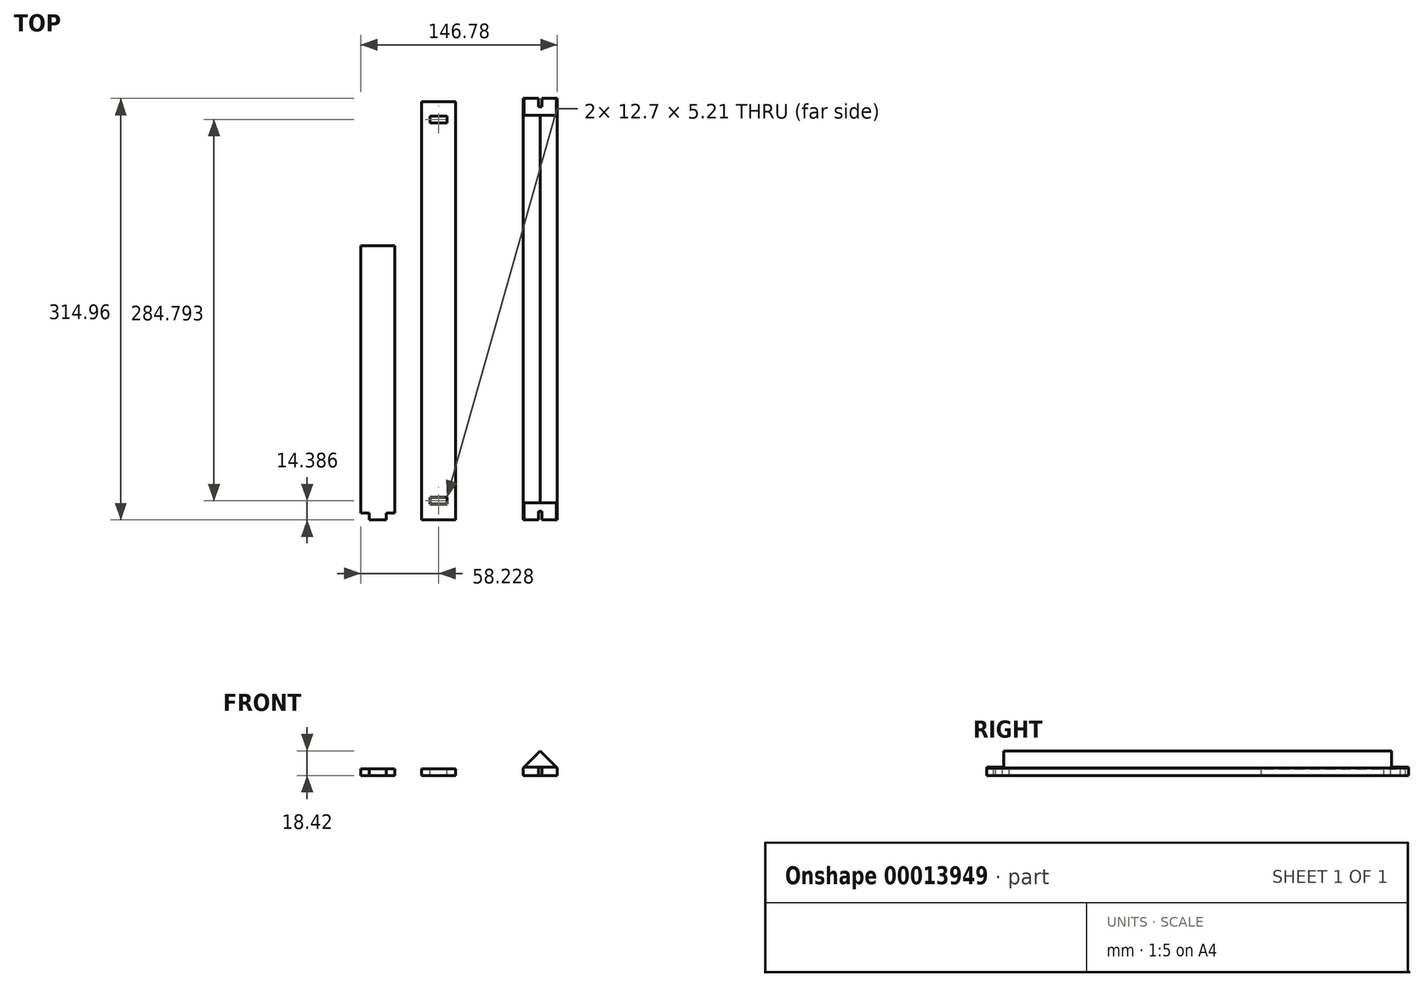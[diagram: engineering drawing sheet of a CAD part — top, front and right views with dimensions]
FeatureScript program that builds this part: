
annotation { "Feature Type Name" : "Feature", "Feature Type Description" : "" }
export const myFeature = defineFeature(function(context is Context, id is Id, definition is map)
    precondition{}
    {
        {
            var Q0;
            Q0=qCreatedBy(makeId("Front.planeOp"),FACE);
            var sketch = newSketch(context, id + "F0", { "sketchPlane" : qUnion([Q0])});
            skLineSegment(sketch, "E0.bottom", {"start": v(0, 0) * mm, "end": v(25.4, 0) * mm});
            skLineSegment(sketch, "E0.left", {"start": v(0, 0) * mm, "end": v(0, 5.72) * mm});
            skLineSegment(sketch, "E0.right", {"start": v(25.4, 0) * mm, "end": v(25.4, 5.72) * mm});
            skLineSegment(sketch, "E1", {"start": v(0, 5.71) * mm, "end": v(12.7, 18.42) * mm});
            skLineSegment(sketch, "E2", {"start": v(25.4, 5.72) * mm, "end": v(12.7, 18.42) * mm});
            skSolve(sketch);
        }
        {
            var Q0;
            Q0=makeQuery(id+"F0.imprint","IMPRINT",FACE,{"disambiguationData":[TD([[makeQuery(id+"F0.imprint","IMPRINT",EDGE,{"derivedFrom":sQuery(id+"F0.wireOp",EDGE,"E0.bottom")}),1.0]])]});
            extrude(context, id + "F1", {"entities" : qUnion([Q0]), "oppositeDirection" : true, "depth" : 314.96 * mm});
        }
        {
            var Q0;
            Q0=qCreatedBy(makeId("Top.planeOp"),FACE);
            cPlane(context, id + "F2", {"entities" : qUnion([Q0]), "cplaneType" : CPlaneType.OFFSET, "offset" : 25.4 * mm, "width" : 152.4 * mm, "height" : 152.4 * mm});
        }
        {
            var Q0;
            Q0=qCreatedBy(id+"F2.planeOp",FACE);
            var sketch = newSketch(context, id + "F3", { "sketchPlane" : qUnion([Q0])});
            skLineSegment(sketch, "E3.bottom", {"start": v(0, 0) * mm, "end": v(25.4, 0) * mm});
            skLineSegment(sketch, "E3.top", {"start": v(0, 12.7) * mm, "end": v(25.4, 12.7) * mm});
            skLineSegment(sketch, "E3.left", {"start": v(0, 0) * mm, "end": v(0, 12.7) * mm});
            skLineSegment(sketch, "E3.right", {"start": v(25.4, 0) * mm, "end": v(25.4, 12.7) * mm});
            skLineSegment(sketch, "E4.0", {"start": v(25.4, 314.96) * mm, "end": v(25.4, 0) * mm});
            skLineSegment(sketch, "E5.0", {"start": v(25.4, 314.96) * mm, "end": v(12.7, 314.96) * mm});
            skLineSegment(sketch, "E6.0", {"start": v(0, 314.96) * mm, "end": v(0, 0) * mm});
            skLineSegment(sketch, "E7.bottom", {"start": v(25.4, 314.96) * mm, "end": v(0, 314.96) * mm});
            skLineSegment(sketch, "E7.top", {"start": v(25.4, 302.26) * mm, "end": v(0, 302.26) * mm});
            skLineSegment(sketch, "E7.left", {"start": v(25.4, 314.96) * mm, "end": v(25.4, 302.26) * mm});
            skLineSegment(sketch, "E7.right", {"start": v(0, 314.96) * mm, "end": v(0, 302.26) * mm});
            skSolve(sketch);
        }
        {
            var Q0;
            Q0=makeQuery(id+"F3.imprint","IMPRINT",FACE,{"disambiguationData":[TD([[makeQuery(id+"F3.imprint","IMPRINT",EDGE,{"derivedFrom":sQuery(id+"F3.wireOp",EDGE,"E7.top")}),-1.0]])]});
            var Q1;
            {var subQ2=sQuery(id+"F3.wireOp",EDGE,"E3.bottom");Q1=makeQuery(id+"F3.imprint","IMPRINT",FACE,{"disambiguationData":[TD([[makeQuery(id+"F3.imprint","IMPRINT",EDGE,{"derivedFrom":subQ2}),1.0]])]});}
            var Q2;
            Q2=qCreatedBy(makeId("Top.planeOp"),FACE);
            extrude(context, id + "F4", {"entities" : qUnion([Q0, Q1]), "operationType" : NewBodyOperationType.REMOVE, "oppositeDirection" : true, "endBoundEntity" : qUnion([Q2]), "depth" : 19.05 * mm});
        }
        {
            var Q0;
            Q0=makeQuery(id+"F1.opExtrude","SWEPT_FACE",FACE,{"disambiguationData":[OSD([sQuery(id+"F0.wireOp",EDGE,"E0.bottom")])]});
            var sketch = newSketch(context, id + "F5", { "sketchPlane" : qUnion([Q0])});
            skLineSegment(sketch, "E8", {"start": v(12.7, 0) * mm, "end": v(12.7, -6.35) * mm, "construction": true});
            skLineSegment(sketch, "E9.rect.bottom", {"start": v(11.43, 0) * mm, "end": v(13.97, 0) * mm});
            skLineSegment(sketch, "E9.rect.top", {"start": v(11.43, -6.35) * mm, "end": v(13.97, -6.35) * mm});
            skLineSegment(sketch, "E9.rect.left", {"start": v(11.43, 0) * mm, "end": v(11.43, -6.35) * mm});
            skLineSegment(sketch, "E9.rect.right", {"start": v(13.97, 0) * mm, "end": v(13.97, -6.35) * mm});
            skPoint(sketch, "E9.rect.middle", {"position": v(12.7, -3.18) * mm});
            skLineSegment(sketch, "E10", {"start": v(12.7, -314.96) * mm, "end": v(12.7, -308.6) * mm, "construction": true});
            skPoint(sketch, "E11.rect.middle", {"position": v(12.7, -314.96) * mm});
            skLineSegment(sketch, "E12.rect.bottom", {"start": v(11.43, -314.96) * mm, "end": v(13.97, -314.96) * mm});
            skLineSegment(sketch, "E12.rect.top", {"start": v(11.43, -308.6) * mm, "end": v(13.97, -308.6) * mm});
            skLineSegment(sketch, "E12.rect.left", {"start": v(11.43, -314.96) * mm, "end": v(11.43, -308.6) * mm});
            skLineSegment(sketch, "E12.rect.right", {"start": v(13.97, -314.96) * mm, "end": v(13.97, -308.6) * mm});
            skPoint(sketch, "E12.rect.middle", {"position": v(12.7, -311.78) * mm});
            skSolve(sketch);
        }
        {
            var Q0;
            Q0=makeQuery(id+"F5.imprint","IMPRINT",FACE,{"disambiguationData":[TD([[makeQuery(id+"F5.imprint","IMPRINT",EDGE,{"derivedFrom":sQuery(id+"F5.wireOp",EDGE,"E12.rect.bottom")}),1.0]])]});
            var Q1;
            Q1=makeQuery(id+"F5.imprint","IMPRINT",FACE,{"disambiguationData":[TD([[makeQuery(id+"F5.imprint","IMPRINT",EDGE,{"derivedFrom":sQuery(id+"F5.wireOp",EDGE,"E9.rect.bottom")}),-1.0]])]});
            extrude(context, id + "F6", {"entities" : qUnion([Q0, Q1]), "operationType" : NewBodyOperationType.REMOVE, "endBound" : BoundingType.THROUGH_ALL, "oppositeDirection" : true, "depth" : 25.4 * mm});
        }
        {
            var Q0;
            Q0=qCreatedBy(makeId("Top.planeOp"),FACE);
            var sketch = newSketch(context, id + "F7", { "sketchPlane" : qUnion([Q0])});
            skLineSegment(sketch, "E13.bottom", {"start": v(-75.85, 0) * mm, "end": v(-50.45, 0) * mm});
            skLineSegment(sketch, "E13.top", {"start": v(-75.85, 312.42) * mm, "end": v(-50.45, 312.42) * mm});
            skLineSegment(sketch, "E13.left", {"start": v(-75.85, 0) * mm, "end": v(-75.85, 312.42) * mm});
            skLineSegment(sketch, "E13.right", {"start": v(-50.45, 0) * mm, "end": v(-50.45, 312.42) * mm});
            skSolve(sketch);
        }
        {
            var Q0;
            Q0=makeQuery(id+"F7.imprint","IMPRINT",FACE,{"disambiguationData":[TD([[makeQuery(id+"F7.imprint","IMPRINT",EDGE,{"derivedFrom":sQuery(id+"F7.wireOp",EDGE,"E13.bottom")}),1.0]])]});
            extrude(context, id + "F8", {"entities" : qUnion([Q0]), "depth" : 5.08 * mm});
        }
        {
            var Q0;
            Q0=makeQuery(id+"F8.opExtrude","CAP_FACE",FACE,{"disambiguationData":[OSD([sQuery(id+"F7.wireOp",EDGE,"E13.bottom"),sQuery(id+"F7.wireOp",EDGE,"E13.top"),sQuery(id+"F7.wireOp",EDGE,"E13.left"),sQuery(id+"F7.wireOp",EDGE,"E13.right")])],"isStart":false});
            var sketch = newSketch(context, id + "F9", { "sketchPlane" : qUnion([Q0])});
            skLineSegment(sketch, "E14.bottom", {"start": v(-69.5, 11.78) * mm, "end": v(-56.8, 11.78) * mm});
            skLineSegment(sketch, "E14.top", {"start": v(-69.5, 16.99) * mm, "end": v(-56.8, 16.99) * mm});
            skLineSegment(sketch, "E14.left", {"start": v(-69.5, 11.78) * mm, "end": v(-69.5, 16.99) * mm});
            skLineSegment(sketch, "E14.right", {"start": v(-56.8, 11.78) * mm, "end": v(-56.8, 16.99) * mm});
            skLineSegment(sketch, "E15.bottom", {"start": v(-69.5, 301.78) * mm, "end": v(-56.8, 301.78) * mm});
            skLineSegment(sketch, "E15.top", {"start": v(-69.5, 296.58) * mm, "end": v(-56.8, 296.58) * mm});
            skLineSegment(sketch, "E15.left", {"start": v(-69.5, 301.78) * mm, "end": v(-69.5, 296.58) * mm});
            skLineSegment(sketch, "E15.right", {"start": v(-56.8, 301.78) * mm, "end": v(-56.8, 296.58) * mm});
            skSolve(sketch);
        }
        {
            var Q0;
            Q0=makeQuery(id+"F9.imprint","IMPRINT",FACE,{"disambiguationData":[TD([[makeQuery(id+"F9.imprint","IMPRINT",EDGE,{"derivedFrom":sQuery(id+"F9.wireOp",EDGE,"E15.bottom")}),-1.0]])]});
            var Q1;
            Q1=makeQuery(id+"F9.imprint","IMPRINT",FACE,{"disambiguationData":[TD([[makeQuery(id+"F9.imprint","IMPRINT",EDGE,{"derivedFrom":sQuery(id+"F9.wireOp",EDGE,"E14.bottom")}),1.0]])]});
            extrude(context, id + "F10", {"entities" : qUnion([Q0, Q1]), "operationType" : NewBodyOperationType.REMOVE, "oppositeDirection" : true, "depth" : 25.4 * mm});
        }
        {
            var Q0;
            Q0=qCreatedBy(makeId("Top.planeOp"),FACE);
            var sketch = newSketch(context, id + "F11", { "sketchPlane" : qUnion([Q0])});
            skLineSegment(sketch, "E16.bottom", {"start": v(-95.98, 0) * mm, "end": v(-121.38, 0) * mm});
            skLineSegment(sketch, "E16.top", {"start": v(-95.98, 205) * mm, "end": v(-121.38, 205) * mm});
            skLineSegment(sketch, "E16.left", {"start": v(-95.98, 0) * mm, "end": v(-95.98, 205) * mm});
            skLineSegment(sketch, "E16.right", {"start": v(-121.38, 0) * mm, "end": v(-121.38, 205) * mm});
            skSolve(sketch);
        }
        {
            var Q0;
            Q0=makeQuery(id+"F11.imprint","IMPRINT",FACE,{"disambiguationData":[TD([[makeQuery(id+"F11.imprint","IMPRINT",EDGE,{"derivedFrom":sQuery(id+"F11.wireOp",EDGE,"E16.bottom")}),-1.0]])]});
            extrude(context, id + "F12", {"entities" : qUnion([Q0]), "depth" : 5.08 * mm});
        }
        {
            var Q0;
            Q0=makeQuery(id+"F12.opExtrude","CAP_FACE",FACE,{"disambiguationData":[OSD([sQuery(id+"F11.wireOp",EDGE,"E16.bottom"),sQuery(id+"F11.wireOp",EDGE,"E16.top"),sQuery(id+"F11.wireOp",EDGE,"E16.left"),sQuery(id+"F11.wireOp",EDGE,"E16.right")])],"isStart":false});
            var sketch = newSketch(context, id + "F13", { "sketchPlane" : qUnion([Q0])});
            skLineSegment(sketch, "E17.bottom", {"start": v(-115.03, 0) * mm, "end": v(-121.38, 0) * mm});
            skLineSegment(sketch, "E17.top", {"start": v(-115.03, 5.08) * mm, "end": v(-121.38, 5.08) * mm});
            skLineSegment(sketch, "E17.left", {"start": v(-115.03, 0) * mm, "end": v(-115.03, 5.08) * mm});
            skLineSegment(sketch, "E17.right", {"start": v(-121.38, 0) * mm, "end": v(-121.38, 5.08) * mm});
            skLineSegment(sketch, "E18.bottom", {"start": v(-102.45, 0) * mm, "end": v(-95.98, 0) * mm});
            skLineSegment(sketch, "E18.top", {"start": v(-102.45, 5.08) * mm, "end": v(-95.98, 5.08) * mm});
            skLineSegment(sketch, "E18.left", {"start": v(-102.45, 0) * mm, "end": v(-102.45, 5.08) * mm});
            skLineSegment(sketch, "E18.right", {"start": v(-95.98, 0) * mm, "end": v(-95.98, 5.08) * mm});
            skSolve(sketch);
        }
        {
            var Q0;
            Q0=makeQuery(id+"F13.imprint","IMPRINT",FACE,{"disambiguationData":[TD([[makeQuery(id+"F13.imprint","IMPRINT",EDGE,{"derivedFrom":sQuery(id+"F13.wireOp",EDGE,"E17.bottom")}),-1.0]])]});
            var Q1;
            Q1=makeQuery(id+"F13.imprint","IMPRINT",FACE,{"disambiguationData":[TD([[makeQuery(id+"F13.imprint","IMPRINT",EDGE,{"derivedFrom":sQuery(id+"F13.wireOp",EDGE,"E18.bottom")}),-1.0]])]});
            extrude(context, id + "F14", {"entities" : qUnion([Q0, Q1]), "operationType" : NewBodyOperationType.REMOVE, "oppositeDirection" : true, "depth" : 25.4 * mm});
        }
    });
